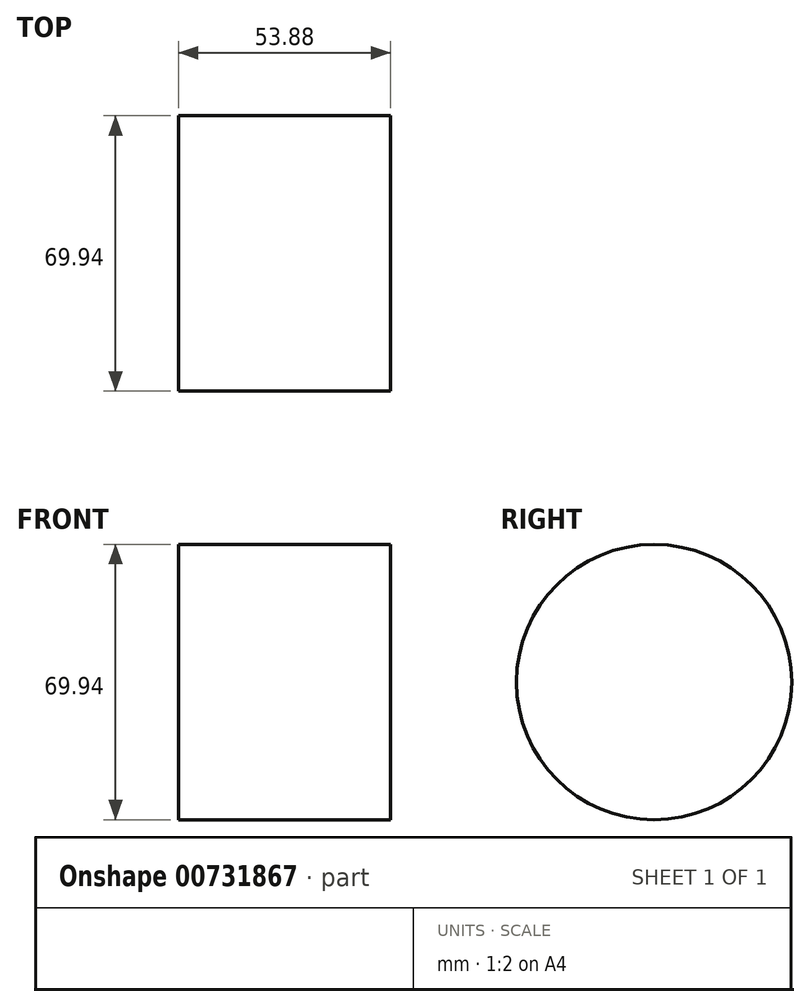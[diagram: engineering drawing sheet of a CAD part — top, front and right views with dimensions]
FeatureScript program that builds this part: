
annotation { "Feature Type Name" : "Feature", "Feature Type Description" : "" }
export const myFeature = defineFeature(function(context is Context, id is Id, definition is map)
    precondition{}
    {
        {
            var Q0;
            Q0=qCreatedBy(makeId("Top.planeOp"),FACE);
            var sketch = newSketch(context, id + "F0", { "sketchPlane" : qUnion([Q0])});
            skLineSegment(sketch, "E0.bottom", {"start": v(0, 0) * mm, "end": v(53.88, 0) * mm});
            skLineSegment(sketch, "E0.top", {"start": v(0, 34.97) * mm, "end": v(53.88, 34.97) * mm});
            skLineSegment(sketch, "E0.left", {"start": v(0, 0) * mm, "end": v(0, 34.97) * mm});
            skLineSegment(sketch, "E0.right", {"start": v(53.88, 0) * mm, "end": v(53.88, 34.97) * mm});
            skSolve(sketch);
        }
        {
            var Q0;
            Q0=makeQuery(id+"F0.imprint","IMPRINT",FACE,{"disambiguationData":[TD([[makeQuery(id+"F0.imprint","IMPRINT",EDGE,{"derivedFrom":sQuery(id+"F0.wireOp",EDGE,"E0.bottom")}),1.0]])]});
            var Q1;
            Q1=sQuery(id+"F0.wireOp",EDGE,"E0.bottom");
            revolve(context, id + "F1", {"surfaceOperationType" : NewSurfaceOperationType.NEW, "entities" : qUnion([Q0]), "axis" : qUnion([Q1]), "revolveType" : RevolveType.FULL});
        }
        {
            var Q0;
            Q0=makeQuery(id+"F1.opRevolve","SWEPT_FACE",FACE,{"disambiguationData":[OSD([sQuery(id+"F0.wireOp",EDGE,"E0.right")])]});
            var sketch = newSketch(context, id + "F2", { "sketchPlane" : qUnion([Q0])});
            skCircle(sketch, "E1", {"center": v(0, 0) * mm, "radius": 27.27 * mm});
            skSolve(sketch);
        }
        {
            var Q0;
            Q0 = qSketchRegion(id + "F2", true);
            extrude(context, id + "F3", {"entities" : qUnion([Q0]), "operationType" : NewBodyOperationType.ADD, "oppositeDirection" : true, "depth" : 25 * mm, "offsetDistance" : 25 * mm});
        }
    });
